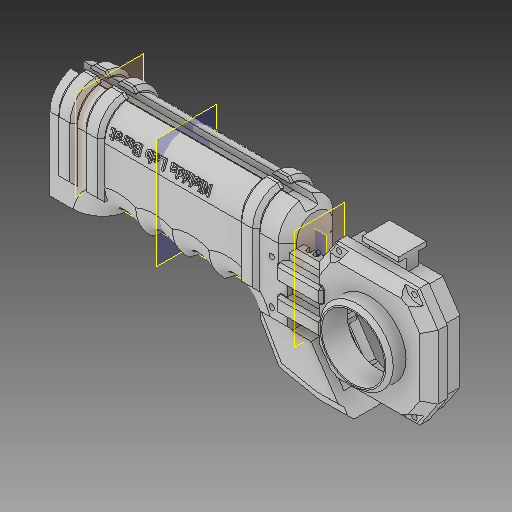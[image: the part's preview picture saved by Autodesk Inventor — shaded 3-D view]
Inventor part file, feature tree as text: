
AUTODESK INVENTOR PART (.ipt)
format: ipt  version: 2018 (Build 220112000, 112)  size: 2,524,160 bytes
history: native  units: mm
features: sketch x35, extrude x33, projected_geometry x20, chamfer x13, other x11, fillet x10, mirror x8, reference x4, pattern_circular x1, pattern_linear x1
ambient origin geometry x8: Origin, YZ Plane, XZ Plane, XY Plane, X Axis, Y Axis, Z Axis, Center Point
bodies: Body1 (feature_tree), Body2 (feature_tree), Body3 (feature_tree), Body4 (feature_tree), Body5 (feature_tree)
feature tree (136):
  other  "ソリッド1"
  extrude  "押し出し1"  Depth=40.0mm
  extrude  "押し出し2"  Depth=14.0mm TaperAngle=0.0deg
  chamfer  "面取り1"  Distance=34.5mm
  extrude  "押し出し3"  Depth=5.0mm TaperAngle=0.0deg
  extrude  "押し出し4"  Depth=2.0mm TaperAngle=45.0deg
  extrude  "押し出し5"  Depth=5.0mm TaperAngle=0.0deg
  pattern_circular  "円形状パターン2"  [2 undecoded]
  extrude  "押し出し6"  Depth=3.0mm
  extrude  "押し出し8"  Depth=10.0mm TaperAngle=0.0deg
  pattern_linear  "矩形状パターン1"  Spacing1=2.0mm  [1 undecoded]
  extrude  "押し出し10"  Depth=3.25mm TaperAngle=0.0deg
  fillet  "フィレット2"  Radius=40.0mm
  extrude  "押し出し12"  Depth=65.0mm
  chamfer  "面取り2"  Distance=65.0mm
  extrude  "押し出し13"  Depth=130.0mm
  mirror  "ミラー1"
  mirror  "ミラー2"
  fillet  "フィレット7"  Radius=55.0mm
  extrude  "押し出し14"  Depth=45.0mm
  extrude  "押し出し15"  Depth=30.0mm TaperAngle=0.0deg
  fillet  "フィレット8"  Radius=48.0mm
  fillet  "フィレット9"  Radius=17.0mm
  extrude  "押し出し16"  Depth=5.0mm
  chamfer  "面取り4"  Distance=125.0mm
  extrude  "押し出し19"  Depth=40.0mm
  chamfer  "面取り5"  Distance=15.0mm
  other  "作業平面1"
  extrude  "押し出し20"  Depth=10.0mm
  extrude  "押し出し21"  Depth=10.0mm
  chamfer  "面取り6"  Distance=15.0mm
  fillet  "フィレット11"  Radius=15.0mm
  extrude  "押し出し22"  Depth=15.0mm
  mirror  "ミラー3"
  chamfer  "面取り10"  Distance=10.0mm
  chamfer  "面取り11"  Distance=10.0mm
  chamfer  "面取り12"  Distance=15.0mm
  chamfer  "面取り13"  Distance=125.0mm
  extrude  "押し出し23"  Depth=15.0mm
  other  "作業平面2"
  mirror  "ミラー4"
  other  "作業平面3"
  mirror  "ミラー5"
  extrude  "押し出し24"  Depth=20.0mm
  fillet  "フィレット14"  Radius=3.0mm
  fillet  "フィレット15"  Radius=5.0mm
  fillet  "フィレット16"  Radius=10.0mm
  chamfer  "面取り14"  Distance=6.0mm
  extrude  "押し出し25"  Depth=5.0mm TaperAngle=0.0deg
  extrude  "押し出し26"  Depth=15.0mm
  extrude  "押し出し27"  Depth=1.5mm
  chamfer  "面取り15"  Distance=3.0mm
  other  "作業平面4"
  mirror  "ミラー6"
  extrude  "押し出し28"  Depth=4.0mm TaperAngle=0.0deg
  fillet  "フィレット17"  Radius=2.0mm
  fillet  "フィレット18"  Radius=2.0mm
  extrude  "押し出し29"  Depth=3.0mm
  extrude  "押し出し30"  Depth=9.0mm
  extrude  "押し出し31"  Depth=3.0mm
  chamfer  "面取り16"  Distance=2.0mm
  chamfer  "面取り17"  Distance=1.5mm Angle=45.0deg
  other  "エンボス1"
  other  "エンボス2"
  extrude  "押し出し32"  Depth=6.0mm TaperAngle=0.0deg
  extrude  "押し出し33"  Depth=10.0mm TaperAngle=45.0deg
  extrude  "押し出し34"  [1 undecoded]
  extrude  "押し出し35"  Depth=3.0mm
  mirror  "ミラー7"
  mirror  "ミラー8"
  extrude  "押し出し36"  Depth=40.0mm
  extrude  "押し出し37"  TaperAngle=60.0deg  [1 undecoded]
  extrude  "押し出し38"  TaperAngle=45.0deg  [1 undecoded]
  sketch  "スケッチ1"
  sketch  "スケッチ2"
  sketch  "スケッチ3"
  sketch  "スケッチ4"
  sketch  "スケッチ5"
  sketch  "スケッチ6"
  sketch  "スケッチ7"
  sketch  "スケッチ8"
  projected_geometry  "投影ループ1"
  sketch  "スケッチ11"
  projected_geometry  "投影ループ3"
  sketch  "スケッチ17"
  projected_geometry  "投影ループ4"
  sketch  "スケッチ18"
  projected_geometry  "投影ループ5"
  sketch  "スケッチ19"
  projected_geometry  "投影ループ6"
  sketch  "スケッチ20"
  projected_geometry  "投影ループ7"
  sketch  "スケッチ21"
  sketch  "スケッチ24"
  sketch  "スケッチ25"
  sketch  "スケッチ26"
  projected_geometry  "投影ループ9"
  sketch  "スケッチ27"
  sketch  "スケッチ28"
  sketch  "スケッチ29"
  sketch  "スケッチ30"
  projected_geometry  "投影ループ10"
  projected_geometry  "投影ループ11"
  projected_geometry  "投影ループ12"
  sketch  "スケッチ31"
  sketch  "スケッチ32"
  projected_geometry  "投影ループ13"
  projected_geometry  "投影ループ14"
  sketch  "スケッチ34"
  projected_geometry  "投影ループ15"
  sketch  "スケッチ35"
  projected_geometry  "投影ループ16"
  sketch  "スケッチ36"
  sketch  "スケッチ37"
  sketch  "スケッチ38"
  sketch  "スケッチ39"
  reference  "参照1"
  reference  "参照2"
  sketch  "スケッチ40"
  reference  "参照3"
  reference  "参照4"
  sketch  "スケッチ41"
  projected_geometry  "投影ループ17"
  projected_geometry  "投影ループ18"
  sketch  "スケッチ42"
  projected_geometry  "投影ループ19"
  sketch  "スケッチ44"
  projected_geometry  "投影ループ20"
  sketch  "スケッチ45"
  projected_geometry  "投影ループ21"
  sketch  "スケッチ46"
  projected_geometry  "投影ループ22"
  parser-record x1  (decoder bookkeeping rows leaked as tree rows — omitted from the tree; the rows remain in map.json)
  other  "shooter.iam"
  other  "toptest:1"
  other  "topcover:1"
note: 6 required parameter values undecoded (feature->parameter linkage not recoverable at this tier; creation-order binding heuristic only, values carry confidence <= 0.55)
note: 1 file-system path scrubbed to <path> (originals preserved in map.json)
